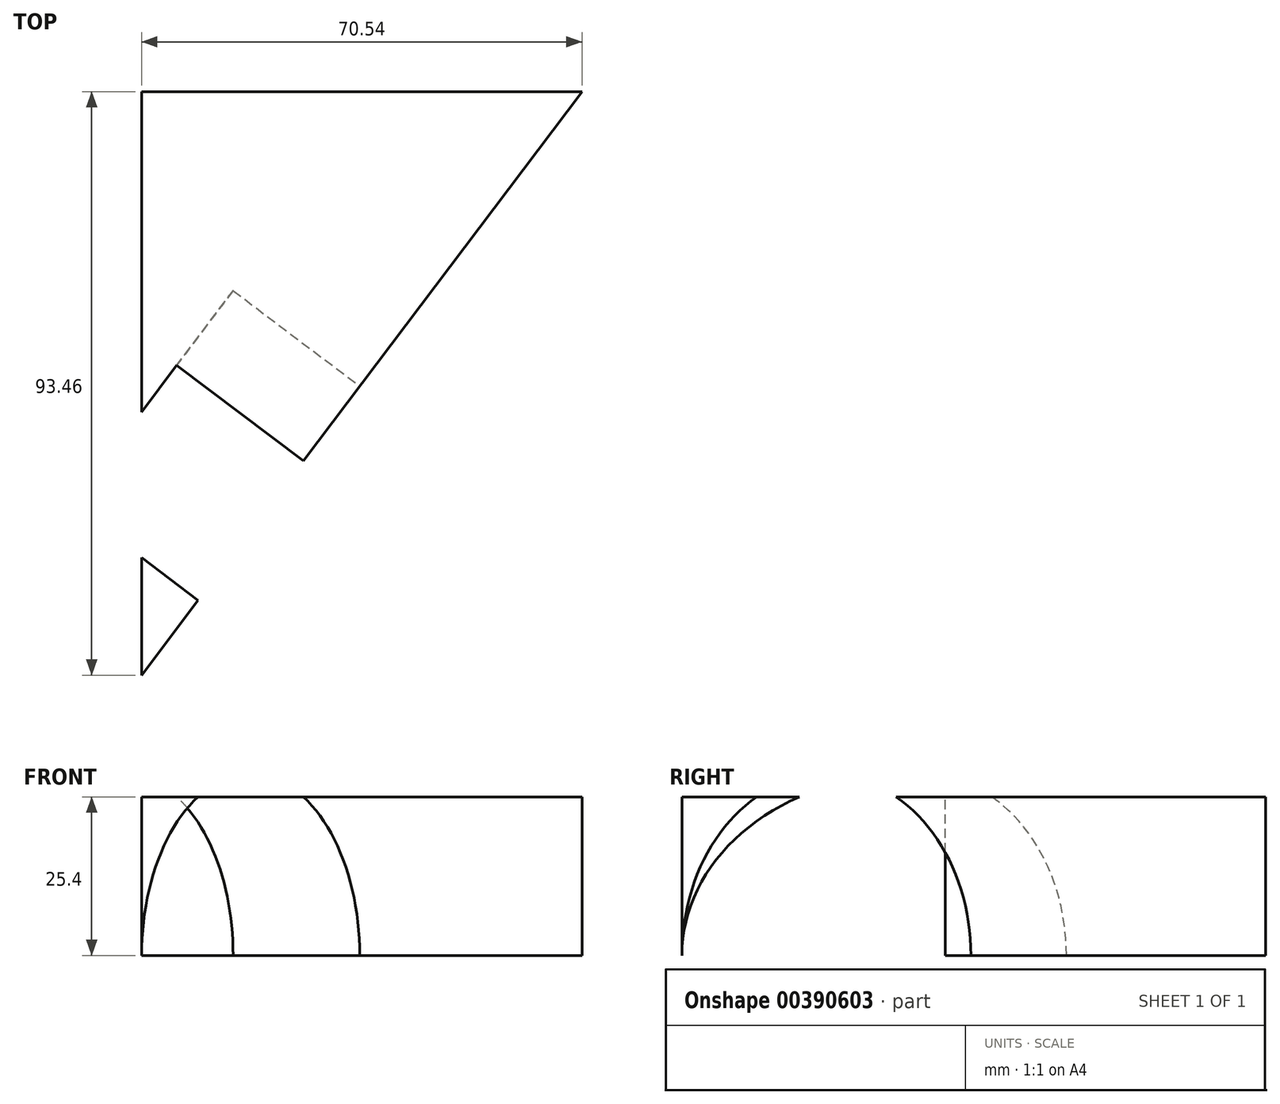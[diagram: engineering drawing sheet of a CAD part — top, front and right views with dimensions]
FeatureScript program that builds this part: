
annotation { "Feature Type Name" : "Feature", "Feature Type Description" : "" }
export const myFeature = defineFeature(function(context is Context, id is Id, definition is map)
    precondition{}
    {
        {
            var Q0;
            Q0=qCreatedBy(makeId("Top.planeOp"),FACE);
            var sketch = newSketch(context, id + "F0", { "sketchPlane" : qUnion([Q0])});
            skLineSegment(sketch, "E0", {"start": v(0, 0) * mm, "end": v(0, 93.46) * mm});
            skLineSegment(sketch, "E1", {"start": v(0, 93.46) * mm, "end": v(70.54, 93.46) * mm});
            skLineSegment(sketch, "E2", {"start": v(70.54, 93.46) * mm, "end": v(70.54, 93.46) * mm});
            skLineSegment(sketch, "E3", {"start": v(0, 0) * mm, "end": v(70.54, 93.46) * mm});
            skSolve(sketch);
        }
        {
            var Q0;
            Q0=makeQuery(id+"F0.imprint","IMPRINT",FACE,{"disambiguationData":[TD([[makeQuery(id+"F0.imprint","IMPRINT",EDGE,{"derivedFrom":sQuery(id+"F0.wireOp",EDGE,"E0")}),-1.0]])]});
            extrude(context, id + "F1", {"entities" : qUnion([Q0]), "depth" : 25.4 * mm});
        }
        {
            var Q0;
            Q0=makeQuery(id+"F1.opExtrude","SWEPT_FACE",FACE,{"disambiguationData":[OSD([sQuery(id+"F0.wireOp",EDGE,"E3")])]});
            var sketch = newSketch(context, id + "F2", { "sketchPlane" : qUnion([Q0])});
            skCircle(sketch, "E4", {"center": v(29, 0) * mm, "radius": 29 * mm});
            skSolve(sketch);
        }
        {
            var Q0;
            {var subQ0=sQuery(id+"F2.wireOp",EDGE,"E4");var subQ1=sQuery(id+"F0.wireOp",EDGE,"E3");var subQ2=makeQuery(id+"F1.opExtrude","CAP_EDGE",EDGE,{"disambiguationData":[OSD([subQ1])],"isStart":true});var subQ4=makeQuery(id+"F2.imprint","INTERSECT",VERTEX,{"derivedFrom":[subQ2,subQ0]});Q0=makeQuery(id+"F2.imprint","IMPRINT",FACE,{"disambiguationData":[TD([[makeQuery(id+"F2.imprint","IMPRINT",EDGE,{"disambiguationData":[TD([[subQ4,1.0]])],"derivedFrom":subQ0}),1.0]])]});}
            var Q1;
            {var subQ0=sQuery(id+"F2.wireOp",EDGE,"E4");var subQ1=sQuery(id+"F0.wireOp",EDGE,"E3");var subQ2=makeQuery(id+"F1.opExtrude","CAP_EDGE",EDGE,{"disambiguationData":[OSD([subQ1])],"isStart":false});var subQ3=makeQuery(id+"F2.imprint","INTERSECT",VERTEX,{"disambiguationData":[OD(0.0)],"derivedFrom":[subQ2,subQ0]});Q1=makeQuery(id+"F2.imprint","IMPRINT",FACE,{"disambiguationData":[TD([[makeQuery(id+"F2.imprint","IMPRINT",EDGE,{"disambiguationData":[TD([[subQ3,1.0]])],"derivedFrom":subQ0}),1.0]])]});}
            var Q2;
            {var subQ0=sQuery(id+"F2.wireOp",EDGE,"E4");var subQ1=makeQuery(id+"F1.opExtrude","CAP_EDGE",EDGE,{"disambiguationData":[OSD([sQuery(id+"F0.wireOp",EDGE,"E3")])],"isStart":false});var subQ2=makeQuery(id+"F2.imprint","INTERSECT",VERTEX,{"disambiguationData":[OD(0.0)],"derivedFrom":[subQ1,subQ0]});Q2=makeQuery(id+"F2.imprint","IMPRINT",FACE,{"disambiguationData":[TD([[makeQuery(id+"F2.imprint","IMPRINT",EDGE,{"disambiguationData":[TD([[subQ2,-1.0]])],"derivedFrom":subQ0}),1.0]])]});}
            extrude(context, id + "F3", {"entities" : qUnion([Q0, Q1, Q2]), "operationType" : NewBodyOperationType.REMOVE, "oppositeDirection" : true, "depth" : 25.4 * mm});
        }
    });
